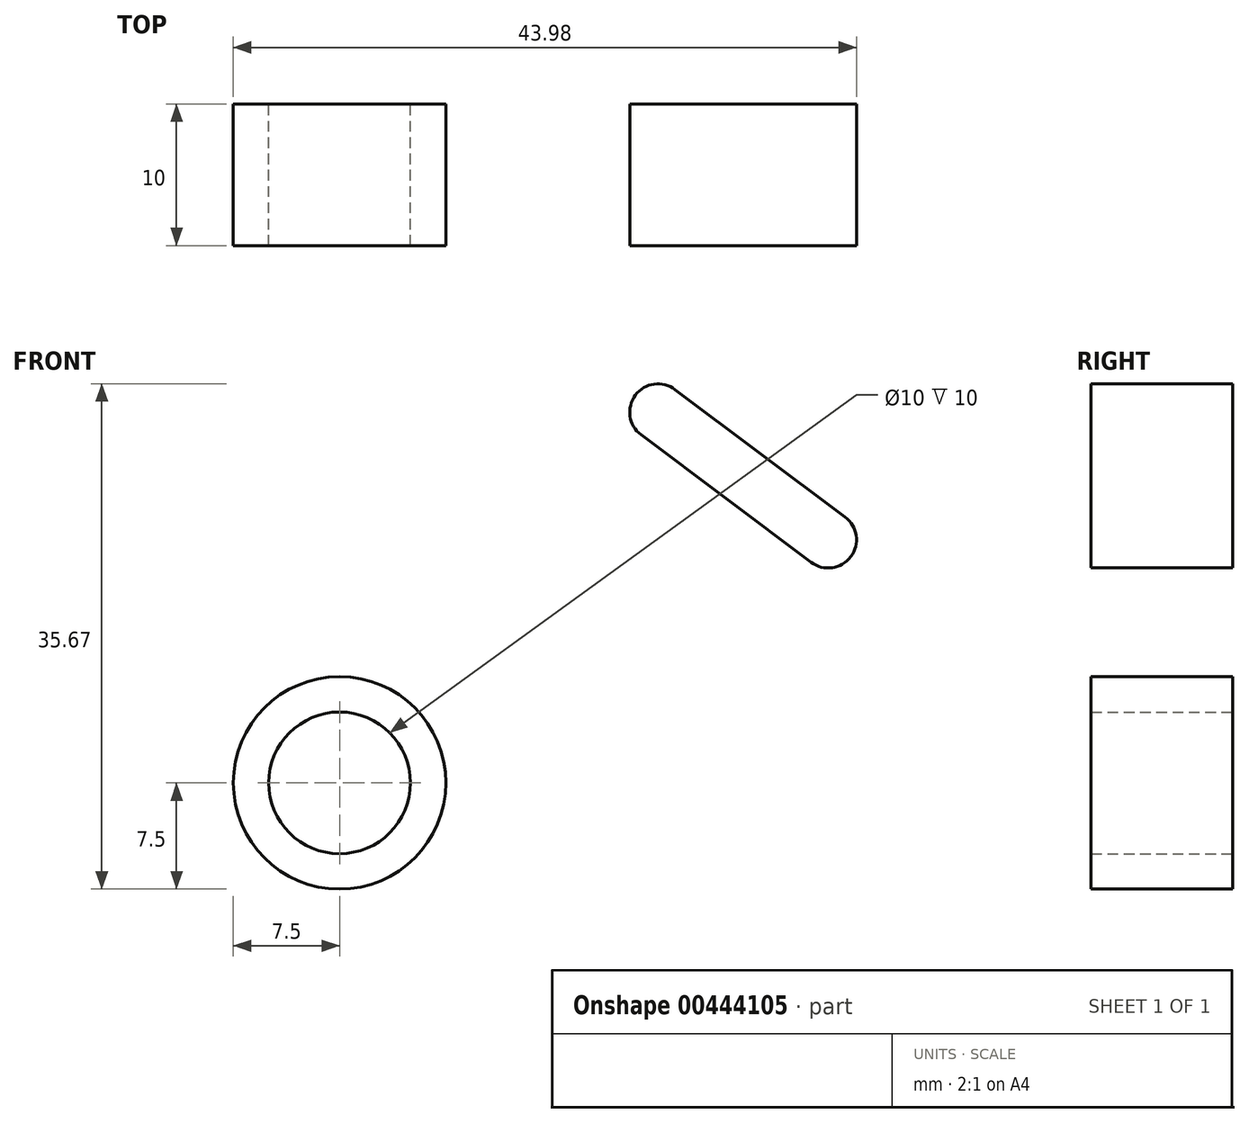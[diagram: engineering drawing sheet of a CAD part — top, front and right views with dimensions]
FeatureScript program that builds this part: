
annotation { "Feature Type Name" : "Feature", "Feature Type Description" : "" }
export const myFeature = defineFeature(function(context is Context, id is Id, definition is map)
    precondition{}
    {
        {
            var Q0;
            Q0=qCreatedBy(makeId("Front.planeOp"),FACE);
            var sketch = newSketch(context, id + "F0", { "sketchPlane" : qUnion([Q0])});
            skLineSegment(sketch, "E0", {"start": v(0, 15) * mm, "end": v(0, -15) * mm, "construction": true});
            skLineSegment(sketch, "E1", {"start": v(1.73, 0) * mm, "end": v(71.73, 0) * mm, "construction": true});
            skCircle(sketch, "E2", {"center": v(0, 15) * mm, "radius": 5 * mm});
            skCircle(sketch, "E3", {"center": v(0, -15) * mm, "radius": 5 * mm});
            skArc(sketch, "E4.0", {"start": v(-7.02, -17.65) * mm, "mid": v(2.65, -22.02) * mm, "end": v(7.02, -12.35) * mm});
            skArc(sketch, "E5.0", {"start": v(7.02, 12.35) * mm, "mid": v(2.65, 22.02) * mm, "end": v(-7.02, 17.65) * mm});
            skArc(sketch, "E6", {"start": v(-7.02, 17.65) * mm, "mid": v(-10.24, 0) * mm, "end": v(-7.02, -17.65) * mm});
            skArc(sketch, "E7", {"start": v(7.02, 12.35) * mm, "mid": v(4.76, 0) * mm, "end": v(7.02, -12.35) * mm});
            skSolve(sketch);
        }
        {
            var Q0;
            Q0=qCreatedBy(makeId("Front.planeOp"),FACE);
            var sketch = newSketch(context, id + "F1", { "sketchPlane" : qUnion([Q0])});
            skCircle(sketch, "E8.0", {"center": v(0, 15) * mm, "radius": 5 * mm});
            skCircle(sketch, "E9", {"center": v(0, 15) * mm, "radius": 7.5 * mm});
            skArc(sketch, "E10", {"start": v(53.83, 34.1) * mm, "mid": v(19.56, 40.76) * mm, "end": v(-6.88, 17.98) * mm});
            skLineSegment(sketch, "E11", {"start": v(53.83, 34.1) * mm, "end": v(60, 29.47) * mm});
            skLineSegment(sketch, "E12", {"start": v(60, 29.47) * mm, "end": v(49.83, 27.1) * mm});
            skArc(sketch, "E13", {"start": v(29.83, 27.1) * mm, "mid": v(16.1, 23) * mm, "end": v(6.88, 12.02) * mm});
            skLineSegment(sketch, "E14", {"start": v(22.48, 41.17) * mm, "end": v(34.48, 32.17) * mm, "construction": true});
            skArc(sketch, "E15", {"start": v(23.68, 42.77) * mm, "mid": v(20.88, 42.37) * mm, "end": v(21.28, 39.57) * mm});
            skArc(sketch, "E16", {"start": v(33.28, 30.57) * mm, "mid": v(36.24, 31.21) * mm, "end": v(35.17, 34.04) * mm});
            skLineSegment(sketch, "E17", {"start": v(33.28, 30.57) * mm, "end": v(21.28, 39.57) * mm});
            skLineSegment(sketch, "E18", {"start": v(23.68, 42.77) * mm, "end": v(36.08, 33.47) * mm});
            skLineSegment(sketch, "E19", {"start": v(36.08, 33.47) * mm, "end": v(40.54, 40.64) * mm, "construction": true});
            skLineSegment(sketch, "E20", {"start": v(29.83, 27.1) * mm, "end": v(30.85, 25.38) * mm});
            skLineSegment(sketch, "E21", {"start": v(30.85, 25.38) * mm, "end": v(31.83, 27.12) * mm});
            skLineSegment(sketch, "E22.1.0.0", {"start": v(31.83, 27.1) * mm, "end": v(32.85, 25.38) * mm});
            skLineSegment(sketch, "E22.1.0.1", {"start": v(32.85, 25.38) * mm, "end": v(33.83, 27.12) * mm});
            skLineSegment(sketch, "E22.2.0.0", {"start": v(33.83, 27.1) * mm, "end": v(34.85, 25.38) * mm});
            skLineSegment(sketch, "E22.2.0.1", {"start": v(34.85, 25.38) * mm, "end": v(35.83, 27.12) * mm});
            skLineSegment(sketch, "E22.3.0.0", {"start": v(35.83, 27.1) * mm, "end": v(36.85, 25.38) * mm});
            skLineSegment(sketch, "E22.3.0.1", {"start": v(36.85, 25.38) * mm, "end": v(37.83, 27.12) * mm});
            skLineSegment(sketch, "E22.4.0.0", {"start": v(37.83, 27.1) * mm, "end": v(38.85, 25.38) * mm});
            skLineSegment(sketch, "E22.4.0.1", {"start": v(38.85, 25.38) * mm, "end": v(39.83, 27.12) * mm});
            skLineSegment(sketch, "E22.5.0.0", {"start": v(39.83, 27.1) * mm, "end": v(40.85, 25.38) * mm});
            skLineSegment(sketch, "E22.5.0.1", {"start": v(40.85, 25.38) * mm, "end": v(41.83, 27.12) * mm});
            skLineSegment(sketch, "E22.6.0.0", {"start": v(41.83, 27.1) * mm, "end": v(42.85, 25.38) * mm});
            skLineSegment(sketch, "E22.6.0.1", {"start": v(42.85, 25.38) * mm, "end": v(43.83, 27.12) * mm});
            skLineSegment(sketch, "E22.7.0.0", {"start": v(43.83, 27.1) * mm, "end": v(44.85, 25.38) * mm});
            skLineSegment(sketch, "E22.7.0.1", {"start": v(44.85, 25.38) * mm, "end": v(45.83, 27.12) * mm});
            skLineSegment(sketch, "E22.8.0.0", {"start": v(45.83, 27.1) * mm, "end": v(46.85, 25.38) * mm});
            skLineSegment(sketch, "E22.8.0.1", {"start": v(46.85, 25.38) * mm, "end": v(47.83, 27.12) * mm});
            skLineSegment(sketch, "E22.9.0.0", {"start": v(47.83, 27.1) * mm, "end": v(48.85, 25.38) * mm});
            skLineSegment(sketch, "E22.9.0.1", {"start": v(48.85, 25.38) * mm, "end": v(49.83, 27.12) * mm});
            skLineSegment(sketch, "E22.direction1", {"start": v(30.85, 25.38) * mm, "end": v(32.85, 25.38) * mm, "construction": true});
            skSolve(sketch);
        }
        {
            var Q0;
            Q0 = qSketchRegion(id + "F1", true);
            extrude(context, id + "F2", {"entities" : qUnion([Q0]), "depth" : 10 * mm});
        }
    });
